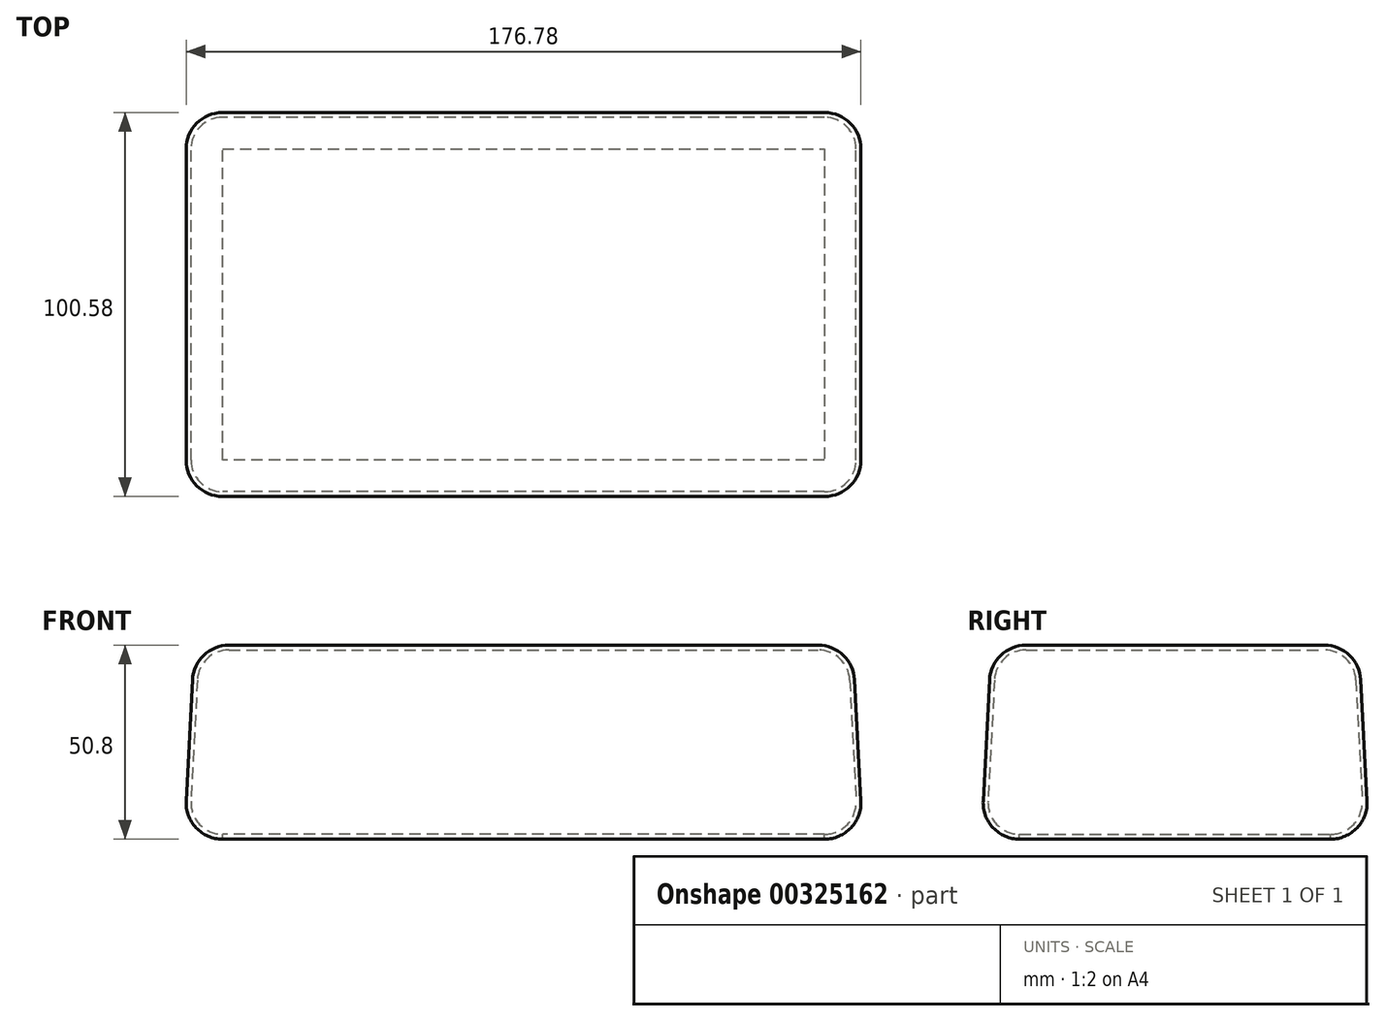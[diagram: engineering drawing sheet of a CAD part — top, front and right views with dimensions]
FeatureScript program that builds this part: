
annotation { "Feature Type Name" : "Feature", "Feature Type Description" : "" }
export const myFeature = defineFeature(function(context is Context, id is Id, definition is map)
    precondition{}
    {
        {
            var Q0;
            Q0=qCreatedBy(makeId("Top.planeOp"),FACE);
            var sketch = newSketch(context, id + "F0", { "sketchPlane" : qUnion([Q0])});
            skLineSegment(sketch, "E0.bottom", {"start": v(-88.9, 50.8) * mm, "end": v(88.9, 50.8) * mm});
            skLineSegment(sketch, "E0.top", {"start": v(-88.9, -50.8) * mm, "end": v(88.9, -50.8) * mm});
            skLineSegment(sketch, "E0.left", {"start": v(-88.9, 50.8) * mm, "end": v(-88.9, -50.8) * mm});
            skLineSegment(sketch, "E0.right", {"start": v(88.9, 50.8) * mm, "end": v(88.9, -50.8) * mm});
            skSolve(sketch);
        }
        {
            var Q0;
            Q0 = qSketchRegion(id + "F0", true);
            extrude(context, id + "F1", {"entities" : qUnion([Q0]), "depth" : 50.8 * mm, "hasDraft" : true, "draftAngle" : 3 * degree, "draftPullDirection" : true});
        }
        {
            var Q0;
            Q0=makeQuery(id+"F1.opExtrude","CAP_EDGE",EDGE,{"disambiguationData":[OSD([sQuery(id+"F0.wireOp",EDGE,"E0.top")])],"isStart":true});
            var Q1;
            Q1=makeQuery(id+"F1.opExtrude","SWEPT_FACE",FACE,{"disambiguationData":[OSD([sQuery(id+"F0.wireOp",EDGE,"E0.top")])]});
            var Q2;
            Q2=makeQuery(id+"F1.opExtrude","CAP_FACE",FACE,{"disambiguationData":[OSD([sQuery(id+"F0.wireOp",EDGE,"E0.bottom"),sQuery(id+"F0.wireOp",EDGE,"E0.top"),sQuery(id+"F0.wireOp",EDGE,"E0.left"),sQuery(id+"F0.wireOp",EDGE,"E0.right")])],"isStart":false});
            var Q3;
            Q3=makeQuery(id+"F1.opExtrude","SWEPT_FACE",FACE,{"disambiguationData":[OSD([sQuery(id+"F0.wireOp",EDGE,"E0.right")])]});
            var Q4;
            Q4=makeQuery(id+"F1.opExtrude","SWEPT_FACE",FACE,{"disambiguationData":[OSD([sQuery(id+"F0.wireOp",EDGE,"E0.bottom")])]});
            var Q5;
            Q5=makeQuery(id+"F1.opExtrude","SWEPT_EDGE",EDGE,{"disambiguationData":[OSD([sQuery(id+"F0.wireOp",EDGE,"E0.bottom"),sQuery(id+"F0.wireOp",EDGE,"E0.left")])]});
            var Q6;
            Q6=makeQuery(id+"F1.opExtrude","CAP_FACE",FACE,{"disambiguationData":[OSD([sQuery(id+"F0.wireOp",EDGE,"E0.bottom"),sQuery(id+"F0.wireOp",EDGE,"E0.top"),sQuery(id+"F0.wireOp",EDGE,"E0.left"),sQuery(id+"F0.wireOp",EDGE,"E0.right")])],"isStart":true});
            fillet(context, id + "F2", {"entities" : qUnion([Q0, Q1, Q2, Q3, Q4, Q5, Q6]), "radius" : 9.52 * mm, "tangentPropagation" : true, "allowEdgeOverflow" : false});
        }
        {
            var Q0;
            Q0=makeQuery(id+"F1.opExtrude","CAP_FACE",FACE,{"disambiguationData":[OSD([sQuery(id+"F0.wireOp",EDGE,"E0.bottom"),sQuery(id+"F0.wireOp",EDGE,"E0.top"),sQuery(id+"F0.wireOp",EDGE,"E0.left"),sQuery(id+"F0.wireOp",EDGE,"E0.right")])],"isStart":true});
            shell(context, id + "F3", {"entities" : qUnion([Q0]), "thickness" : 1.27 * mm});
        }
    });
